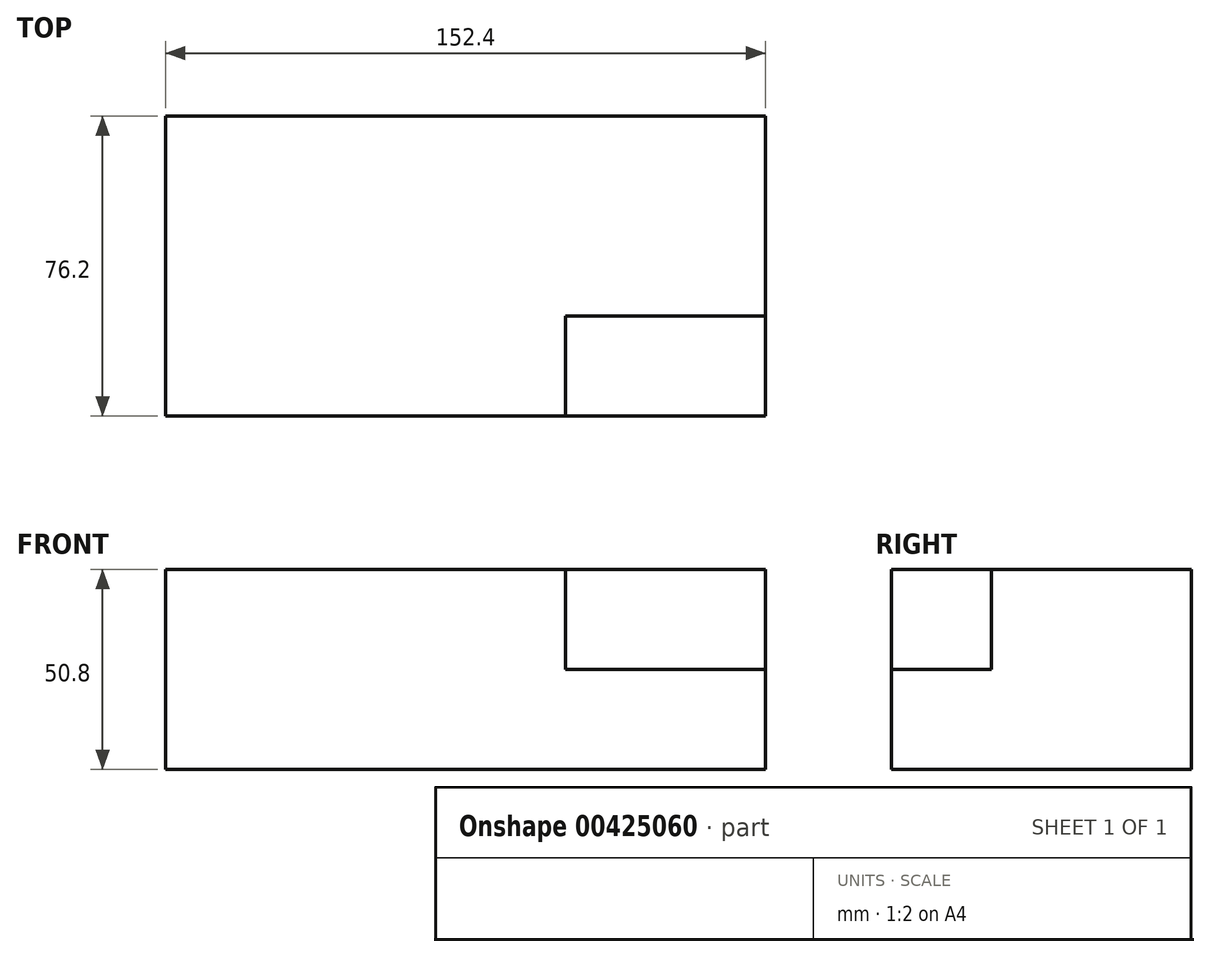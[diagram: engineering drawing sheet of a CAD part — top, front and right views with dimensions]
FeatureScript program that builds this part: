
annotation { "Feature Type Name" : "Feature", "Feature Type Description" : "" }
export const myFeature = defineFeature(function(context is Context, id is Id, definition is map)
    precondition{}
    {
        {
            var Q0;
            Q0=qCreatedBy(makeId("Top.planeOp"),FACE);
            var sketch = newSketch(context, id + "F0", { "sketchPlane" : qUnion([Q0])});
            skLineSegment(sketch, "E0", {"start": v(0, 0) * mm, "end": v(152.4, 0) * mm});
            skLineSegment(sketch, "E1", {"start": v(152.4, 0) * mm, "end": v(152.4, 76.2) * mm});
            skLineSegment(sketch, "E2", {"start": v(152.4, 76.2) * mm, "end": v(0, 76.2) * mm});
            skLineSegment(sketch, "E3", {"start": v(0, 76.2) * mm, "end": v(0, 0) * mm});
            skSolve(sketch);
        }
        {
            var Q0;
            Q0 = qSketchRegion(id + "F0", true);
            extrude(context, id + "F1", {"entities" : qUnion([Q0]), "depth" : 50.8 * mm});
        }
        {
            var Q0;
            Q0=makeQuery(id+"F1.opExtrude","SWEPT_FACE",FACE,{"disambiguationData":[OSD([sQuery(id+"F0.wireOp",EDGE,"E0")])]});
            var sketch = newSketch(context, id + "F2", { "sketchPlane" : qUnion([Q0])});
            skLineSegment(sketch, "E4", {"start": v(152.4, 50.8) * mm, "end": v(101.6, 50.8) * mm});
            skLineSegment(sketch, "E5", {"start": v(101.6, 50.8) * mm, "end": v(101.6, 25.4) * mm});
            skLineSegment(sketch, "E6", {"start": v(101.6, 25.4) * mm, "end": v(152.4, 25.4) * mm});
            skLineSegment(sketch, "E7", {"start": v(152.4, 25.4) * mm, "end": v(152.4, 50.8) * mm});
            skSolve(sketch);
        }
        {
            var Q0;
            Q0 = qSketchRegion(id + "F2", true);
            extrude(context, id + "F3", {"entities" : qUnion([Q0]), "operationType" : NewBodyOperationType.REMOVE, "oppositeDirection" : true, "depth" : 25.4 * mm});
        }
    });
